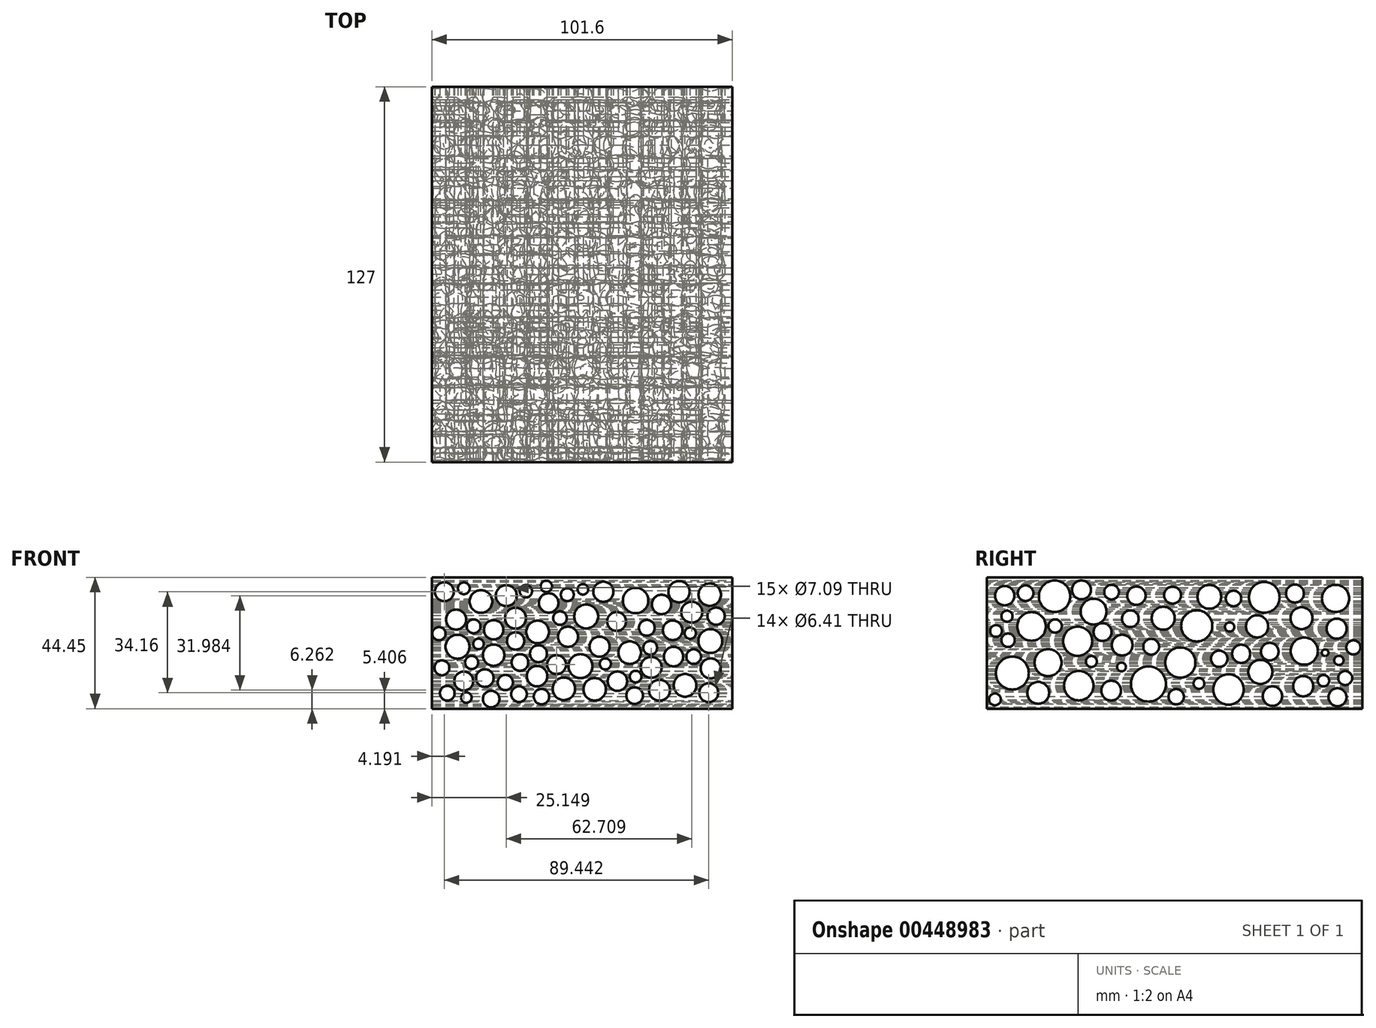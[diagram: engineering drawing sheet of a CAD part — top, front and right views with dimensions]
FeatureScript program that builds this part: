
annotation { "Feature Type Name" : "Feature", "Feature Type Description" : "" }
export const myFeature = defineFeature(function(context is Context, id is Id, definition is map)
    precondition{}
    {
        {
            var Q0;
            Q0=qCreatedBy(makeId("Front.planeOp"),FACE);
            var sketch = newSketch(context, id + "F0", { "sketchPlane" : qUnion([Q0])});
            skLineSegment(sketch, "E0.bottom", {"start": v(-47.65, 23.5) * mm, "end": v(53.95, 23.5) * mm});
            skLineSegment(sketch, "E0.top", {"start": v(-47.65, -20.95) * mm, "end": v(53.95, -20.95) * mm});
            skLineSegment(sketch, "E0.left", {"start": v(-47.65, 23.5) * mm, "end": v(-47.65, -20.95) * mm});
            skLineSegment(sketch, "E0.right", {"start": v(53.95, 23.5) * mm, "end": v(53.95, -20.95) * mm});
            skSolve(sketch);
        }
        {
            var Q0;
            Q0 = qSketchRegion(id + "F0", true);
            extrude(context, id + "F1", {"entities" : qUnion([Q0]), "endBound" : BoundingType.SYMMETRIC, "depth" : 127 * mm});
        }
        {
            var Q0;
            Q0=makeQuery(id+"F1.opExtrude","SWEPT_FACE",FACE,{"disambiguationData":[OSD([sQuery(id+"F0.wireOp",EDGE,"E0.right")])]});
            var sketch = newSketch(context, id + "F2", { "sketchPlane" : qUnion([Q0])});
            skCircle(sketch, "E1", {"center": v(-57.46, 17.28) * mm, "radius": 3.28 * mm});
            skCircle(sketch, "E2", {"center": v(-48.37, 6.89) * mm, "radius": 4.84 * mm});
            skCircle(sketch, "E3", {"center": v(-27.4, 11.9) * mm, "radius": 4.38 * mm});
            skCircle(sketch, "E4", {"center": v(-32.78, 1.87) * mm, "radius": 4.93 * mm});
            skCircle(sketch, "E5", {"center": v(-40.57, 17.1) * mm, "radius": 5.31 * mm});
            skCircle(sketch, "E6", {"center": v(-54.86, -8.9) * mm, "radius": 5.57 * mm});
            skCircle(sketch, "E7", {"center": v(-12.92, 17.28) * mm, "radius": 3.11 * mm});
            skCircle(sketch, "E8", {"center": v(-17.74, 0.57) * mm, "radius": 3.52 * mm});
            skCircle(sketch, "E9", {"center": v(-3.82, 9.67) * mm, "radius": 3.9 * mm});
            skCircle(sketch, "E10", {"center": v(-14.96, 9.48) * mm, "radius": 2.83 * mm});
            skCircle(sketch, "E11", {"center": v(-28.14, -5) * mm, "radius": 1.87 * mm});
            skCircle(sketch, "E12", {"center": v(-42.8, -5.36) * mm, "radius": 4.58 * mm});
            skCircle(sketch, "E13", {"center": v(-32.4, -13.16) * mm, "radius": 4.99 * mm});
            skCircle(sketch, "E14", {"center": v(1.93, -5.36) * mm, "radius": 5.12 * mm});
            skCircle(sketch, "E15", {"center": v(-17.93, -6.85) * mm, "radius": 1.5 * mm});
            skCircle(sketch, "E16", {"center": v(-8.83, -12.6) * mm, "radius": 5.94 * mm});
            skCircle(sketch, "E17", {"center": v(11.77, 16.9) * mm, "radius": 4.02 * mm});
            skCircle(sketch, "E18", {"center": v(-0.67, 17.46) * mm, "radius": 2.88 * mm});
            skCircle(sketch, "E19", {"center": v(7.5, 7.07) * mm, "radius": 5.28 * mm});
            skCircle(sketch, "E20", {"center": v(30.33, 16.72) * mm, "radius": 5.2 * mm});
            skCircle(sketch, "E21", {"center": v(18.64, 6.7) * mm, "radius": 1.57 * mm});
            skCircle(sketch, "E22", {"center": v(19.93, 16.35) * mm, "radius": 2.62 * mm});
            skCircle(sketch, "E23", {"center": v(15.1, -4.07) * mm, "radius": 2.78 * mm});
            skCircle(sketch, "E24", {"center": v(8.24, -12.42) * mm, "radius": 1.84 * mm});
            skCircle(sketch, "E25", {"center": v(-7.9, 0.02) * mm, "radius": 2.68 * mm});
            skCircle(sketch, "E26", {"center": v(-21.46, -14.83) * mm, "radius": 3.35 * mm});
            skCircle(sketch, "E27", {"center": v(43.88, -1.47) * mm, "radius": 4.6 * mm});
            skCircle(sketch, "E28", {"center": v(27.92, 6.89) * mm, "radius": 3.76 * mm});
            skCircle(sketch, "E29", {"center": v(29.03, -8.52) * mm, "radius": 4.07 * mm});
            skCircle(sketch, "E30", {"center": v(42.95, 9.67) * mm, "radius": 3.71 * mm});
            skCircle(sketch, "E31", {"center": v(40.72, 18.02) * mm, "radius": 3.04 * mm});
            skCircle(sketch, "E32", {"center": v(43.5, -13.35) * mm, "radius": 3.42 * mm});
            skCircle(sketch, "E33", {"center": v(32.18, -1.65) * mm, "radius": 3 * mm});
            skCircle(sketch, "E34", {"center": v(54.46, 16.35) * mm, "radius": 4.61 * mm});
            skCircle(sketch, "E35", {"center": v(54.83, 6.14) * mm, "radius": 3.4 * mm});
            skCircle(sketch, "E36", {"center": v(55.57, -4.62) * mm, "radius": 1.57 * mm});
            skCircle(sketch, "E37", {"center": v(50.93, -2.02) * mm, "radius": 1.13 * mm});
            skCircle(sketch, "E38", {"center": v(50.37, -11.49) * mm, "radius": 1.94 * mm});
            skCircle(sketch, "E39", {"center": v(33.11, -16.69) * mm, "radius": 3.3 * mm});
            skCircle(sketch, "E40", {"center": v(18.26, -14.46) * mm, "radius": 5.16 * mm});
            skCircle(sketch, "E41", {"center": v(22.53, -2.4) * mm, "radius": 3.07 * mm});
            skCircle(sketch, "E42", {"center": v(-60.39, 5.35) * mm, "radius": 2 * mm});
            skCircle(sketch, "E43", {"center": v(-50.38, 18.13) * mm, "radius": 2.65 * mm});
            skCircle(sketch, "E44", {"center": v(-56.68, 10.35) * mm, "radius": 1.89 * mm});
            skCircle(sketch, "E45", {"center": v(-56.31, 2.2) * mm, "radius": 2.3 * mm});
            skCircle(sketch, "E46", {"center": v(-46.12, -15.59) * mm, "radius": 3.7 * mm});
            skCircle(sketch, "E47", {"center": v(0.56, -16.88) * mm, "radius": 2.6 * mm});
            skCircle(sketch, "E48", {"center": v(-21.3, 18.5) * mm, "radius": 2.5 * mm});
            skCircle(sketch, "E49", {"center": v(-31.49, 19.24) * mm, "radius": 3.2 * mm});
            skCircle(sketch, "E50", {"center": v(-40.38, 7.01) * mm, "radius": 2.26 * mm});
            skCircle(sketch, "E51", {"center": v(-60.76, -17.8) * mm, "radius": 2 * mm});
            skCircle(sketch, "E52", {"center": v(55.12, -17.07) * mm, "radius": 3.04 * mm});
            skCircle(sketch, "E53", {"center": v(57.7, -10.58) * mm, "radius": 2.37 * mm});
            skCircle(sketch, "E54", {"center": v(60.49, -0.21) * mm, "radius": 2.4 * mm});
            skCircle(sketch, "E55", {"center": v(-24.35, 4.97) * mm, "radius": 3.04 * mm});
            skSolve(sketch);
        }
        {
            var Q0;
            Q0 = qSketchRegion(id + "F2", true);
            extrude(context, id + "F3", {"entities" : qUnion([Q0]), "operationType" : NewBodyOperationType.REMOVE, "endBound" : BoundingType.THROUGH_ALL, "oppositeDirection" : true, "depth" : 25.4 * mm});
        }
        {
            var Q0;
            Q0=makeQuery(id+"F1.opExtrude","CAP_FACE",FACE,{"disambiguationData":[OSD([sQuery(id+"F0.wireOp",EDGE,"E0.bottom"),sQuery(id+"F0.wireOp",EDGE,"E0.top"),sQuery(id+"F0.wireOp",EDGE,"E0.left"),sQuery(id+"F0.wireOp",EDGE,"E0.right")])],"isStart":false});
            var sketch = newSketch(context, id + "F4", { "sketchPlane" : qUnion([Q0])});
            skCircle(sketch, "E56", {"center": v(-43.46, 18.62) * mm, "radius": 3.2 * mm});
            skCircle(sketch, "E57", {"center": v(-31.08, 15.32) * mm, "radius": 3.84 * mm});
            skCircle(sketch, "E58", {"center": v(-39.5, 9.2) * mm, "radius": 3.4 * mm});
            skCircle(sketch, "E59", {"center": v(-39, 0) * mm, "radius": 4.05 * mm});
            skCircle(sketch, "E60", {"center": v(-26.8, 5.74) * mm, "radius": 3.29 * mm});
            skCircle(sketch, "E61", {"center": v(-22.5, 17.3) * mm, "radius": 3.54 * mm});
            skCircle(sketch, "E62", {"center": v(-5.5, -6.06) * mm, "radius": 3.2 * mm});
            skCircle(sketch, "E63", {"center": v(-11.92, 5.03) * mm, "radius": 3.84 * mm});
            skCircle(sketch, "E64", {"center": v(-1.65, 3.4) * mm, "radius": 3.4 * mm});
            skCircle(sketch, "E65", {"center": v(4.51, 10.26) * mm, "radius": 4.05 * mm});
            skCircle(sketch, "E66", {"center": v(-8.18, 14.83) * mm, "radius": 3.29 * mm});
            skCircle(sketch, "E67", {"center": v(-19.38, 9.7) * mm, "radius": 3.54 * mm});
            skCircle(sketch, "E68", {"center": v(14.8, 8.55) * mm, "radius": 3.2 * mm});
            skCircle(sketch, "E69", {"center": v(37.95, -13.06) * mm, "radius": 3.84 * mm});
            skCircle(sketch, "E70", {"center": v(46.61, -7.3) * mm, "radius": 3.4 * mm});
            skCircle(sketch, "E71", {"center": v(46.5, 1.92) * mm, "radius": 4.05 * mm});
            skCircle(sketch, "E72", {"center": v(34.06, -3.32) * mm, "radius": 3.29 * mm});
            skCircle(sketch, "E73", {"center": v(29.3, -14.69) * mm, "radius": 3.54 * mm});
            skCircle(sketch, "E74", {"center": v(-36.9, -11.62) * mm, "radius": 3.2 * mm});
            skCircle(sketch, "E75", {"center": v(19.22, -2) * mm, "radius": 3.84 * mm});
            skCircle(sketch, "E76", {"center": v(9.03, 0.05) * mm, "radius": 3.4 * mm});
            skCircle(sketch, "E77", {"center": v(2.6, -6.55) * mm, "radius": 4.05 * mm});
            skCircle(sketch, "E78", {"center": v(15.1, -11.64) * mm, "radius": 3.29 * mm});
            skCircle(sketch, "E79", {"center": v(26.5, -6.97) * mm, "radius": 3.54 * mm});
            skCircle(sketch, "E80", {"center": v(-26.8, -2.84) * mm, "radius": 3.62 * mm});
            skCircle(sketch, "E81", {"center": v(-19.37, 1.95) * mm, "radius": 2.94 * mm});
            skCircle(sketch, "E82", {"center": v(-29.76, -10.6) * mm, "radius": 2.99 * mm});
            skCircle(sketch, "E83", {"center": v(-17.88, -5.31) * mm, "radius": 2.81 * mm});
            skCircle(sketch, "E84", {"center": v(-22.83, -12.08) * mm, "radius": 2.58 * mm});
            skCircle(sketch, "E85", {"center": v(-44.28, -7.13) * mm, "radius": 2.52 * mm});
            skCircle(sketch, "E86", {"center": v(-12.1, -9.93) * mm, "radius": 3.48 * mm});
            skCircle(sketch, "E87", {"center": v(-11.6, -2.34) * mm, "radius": 2.86 * mm});
            skCircle(sketch, "E88", {"center": v(-1.87, 17.63) * mm, "radius": 2.2 * mm});
            skCircle(sketch, "E89", {"center": v(-15.9, 18.78) * mm, "radius": 2.1 * mm});
            skCircle(sketch, "E90", {"center": v(10.34, 18.62) * mm, "radius": 3.4 * mm});
            skCircle(sketch, "E91", {"center": v(21.23, 15.65) * mm, "radius": 4.3 * mm});
            skCircle(sketch, "E92", {"center": v(25.03, 6.4) * mm, "radius": 2.69 * mm});
            skCircle(sketch, "E93", {"center": v(26.18, -0.36) * mm, "radius": 2.33 * mm});
            skCircle(sketch, "E94", {"center": v(33.77, 5.58) * mm, "radius": 3.3 * mm});
            skCircle(sketch, "E95", {"center": v(29.98, 14.33) * mm, "radius": 3.28 * mm});
            skCircle(sketch, "E96", {"center": v(35.92, 18.62) * mm, "radius": 3.62 * mm});
            skCircle(sketch, "E97", {"center": v(40.2, 11.69) * mm, "radius": 3.54 * mm});
            skCircle(sketch, "E98", {"center": v(46.31, 17.63) * mm, "radius": 3.8 * mm});
            skCircle(sketch, "E99", {"center": v(48.46, 10.37) * mm, "radius": 2.92 * mm});
            skCircle(sketch, "E100", {"center": v(11, -5.8) * mm, "radius": 1.88 * mm});
            skCircle(sketch, "E101", {"center": v(-3.03, -14.22) * mm, "radius": 3.8 * mm});
            skCircle(sketch, "E102", {"center": v(7.37, -14.39) * mm, "radius": 3.8 * mm});
            skCircle(sketch, "E103", {"center": v(-18.21, -16.04) * mm, "radius": 2.66 * mm});
            skCircle(sketch, "E104", {"center": v(-10.62, -16.86) * mm, "radius": 2.6 * mm});
            skCircle(sketch, "E105", {"center": v(-27.62, -17.69) * mm, "radius": 2.8 * mm});
            skCircle(sketch, "E106", {"center": v(-42.47, -15.7) * mm, "radius": 2.5 * mm});
            skCircle(sketch, "E107", {"center": v(-36.03, -17.2) * mm, "radius": 1.78 * mm});
            skCircle(sketch, "E108", {"center": v(-34.22, -5.31) * mm, "radius": 2.22 * mm});
            skCircle(sketch, "E109", {"center": v(-33.56, 6.9) * mm, "radius": 2.33 * mm});
            skCircle(sketch, "E110", {"center": v(-31.9, 0.96) * mm, "radius": 1.78 * mm});
            skCircle(sketch, "E111", {"center": v(20.9, -16.53) * mm, "radius": 2.82 * mm});
            skCircle(sketch, "E112", {"center": v(21.23, -10.1) * mm, "radius": 1.98 * mm});
            skCircle(sketch, "E113", {"center": v(-4.35, 9.7) * mm, "radius": 2.3 * mm});
            skCircle(sketch, "E114", {"center": v(45.98, -15.54) * mm, "radius": 3.2 * mm});
            skCircle(sketch, "E115", {"center": v(40.87, -3.33) * mm, "radius": 2.48 * mm});
            skCircle(sketch, "E116", {"center": v(39.71, 4.59) * mm, "radius": 1.93 * mm});
            skCircle(sketch, "E117", {"center": v(-45.27, 4.42) * mm, "radius": 2.24 * mm});
            skCircle(sketch, "E118", {"center": v(-36.86, 19.77) * mm, "radius": 1.99 * mm});
            skCircle(sketch, "E119", {"center": v(3.4, 19.44) * mm, "radius": 1.78 * mm});
            skCircle(sketch, "E120", {"center": v(-8.97, 20.43) * mm, "radius": 1.93 * mm});
            skSolve(sketch);
        }
        {
            var Q0;
            Q0 = qSketchRegion(id + "F4", true);
            extrude(context, id + "F5", {"entities" : qUnion([Q0]), "operationType" : NewBodyOperationType.REMOVE, "endBound" : BoundingType.THROUGH_ALL, "oppositeDirection" : true, "depth" : 25.4 * mm});
        }
        {
            var Q0;
            Q0=makeQuery(id+"F1.opExtrude","SWEPT_FACE",FACE,{"disambiguationData":[OSD([sQuery(id+"F0.wireOp",EDGE,"E0.bottom")])]});
            cPlane(context, id + "F6", {"entities" : qUnion([Q0]), "cplaneType" : CPlaneType.OFFSET, "offset" : 3.8 * mm, "oppositeDirection" : true, "width" : 152.4 * mm, "height" : 152.4 * mm});
        }
    });
